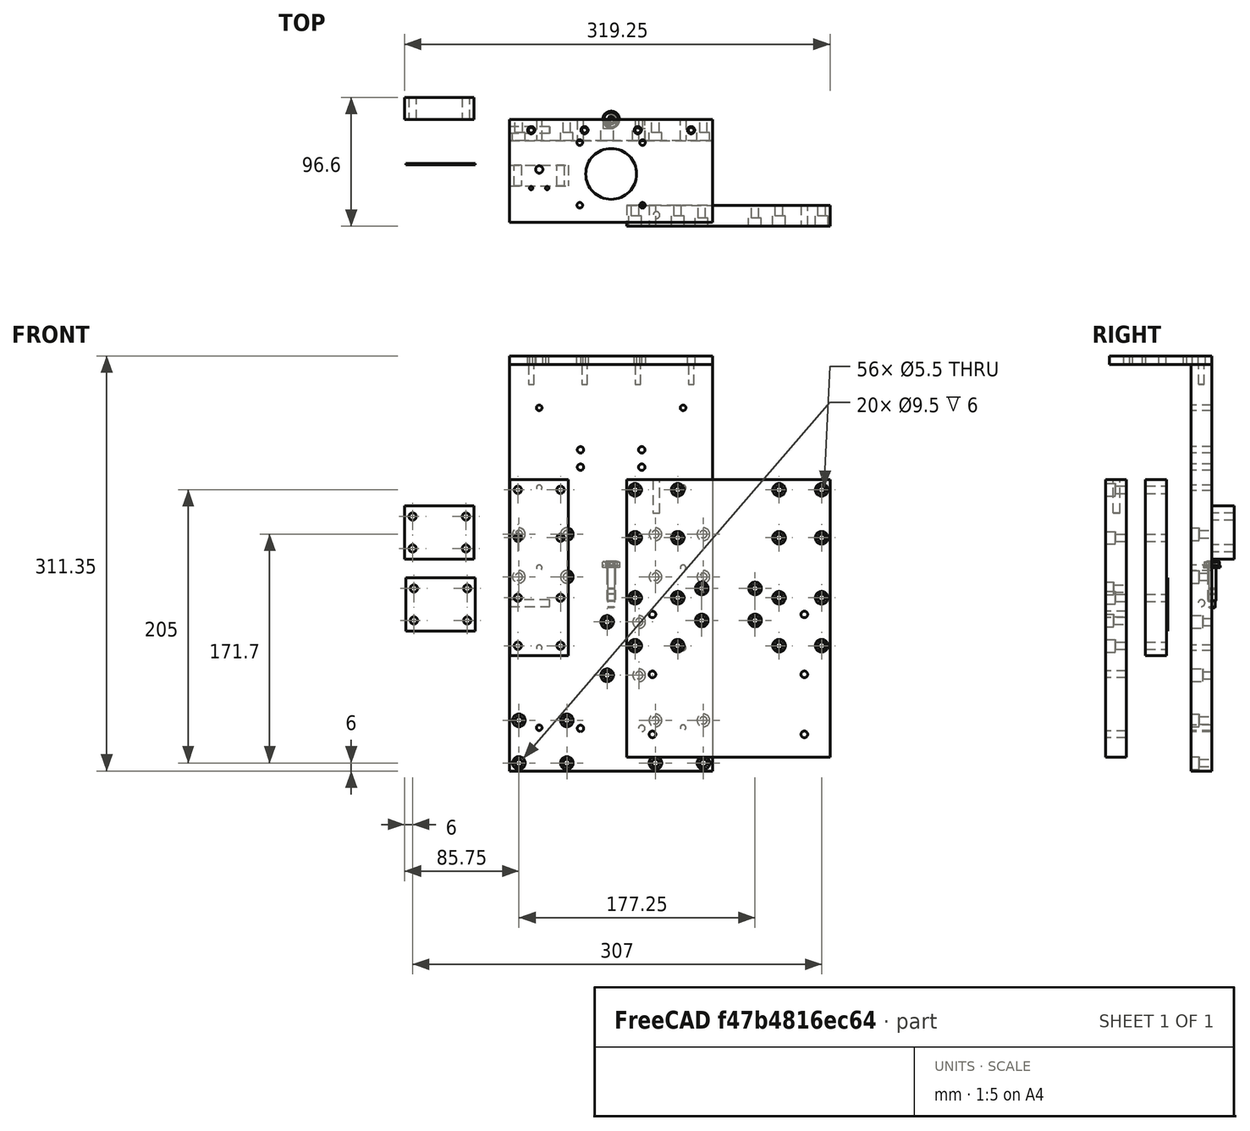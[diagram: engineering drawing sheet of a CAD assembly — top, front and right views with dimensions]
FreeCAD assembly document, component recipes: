
FREECAD ASSEMBLY — COMPONENT RECIPES ("Z axis plates")

This assembly document has 16 components, labeled P0..P15 below (a component is one placed body or linked part). 6 of them carry a construction recipe — the FreeCAD feature program that regenerates the part from scratch, quoted from this document or its linked companion documents; the rest are supplied as boundary geometry only. No exploded tour is included for this assembly.
COMPONENT P0 — recipe-attached ("Link(Backplate)", modeled in this document).
Construction recipe (the document's own serialized feature program — sketch geometry with constraints, then the solid features built on it; lengths are millimeters unless a unit is written):

FEATURE [Sketcher::SketchObject] Sketch
  FullyConstrained = true
  MapMode = 5
  Placement = pos=(0,0,0) rot=(1,0,0;1.5708rad)
  Support = -> [XZ_Plane]
  sketch-geometry (4):
    g0: LineSegment StartX=-76.25 StartY=152.5 StartZ=0 EndX=76.25 EndY=152.5 EndZ=0
    g1: LineSegment StartX=76.25 StartY=152.5 StartZ=0 EndX=76.25 EndY=-152.5 EndZ=0
    g2: LineSegment StartX=76.25 StartY=-152.5 StartZ=0 EndX=-76.25 EndY=-152.5 EndZ=0
    g3: LineSegment StartX=-76.25 StartY=-152.5 StartZ=0 EndX=-76.25 EndY=152.5 EndZ=0
  constraints (11):
    c: Coincident(g0,g1)
    c: Coincident(g1,g2)
    c: Coincident(g2,g3)
    c: Coincident(g3,g0)
    c: Horizontal(g0)
    c: Horizontal(g2)
    c: Vertical(g1)
    c: Vertical(g3)
    c: Symmetric(g1,g0,g-1)
    c: DistanceX(g0,g0) = 152.5
    c: DistanceY(g1,g1) = 305
FEATURE [PartDesign::Pad] Pad
  ClaimChildren = false
  Direction = (1,1,1)
  Fit = 0
  FitJoin = 0
  InnerFit = 0
  InnerFitJoin = 0
  InnerTaperAngle = 0
  InnerTaperAngleRev = 0
  Length = 15.7
  Length2 = 100
  Linearize = true
  NewSolid = false
  Placement = pos=(0,0,0) rot=(1,0,0;1.5708rad)
  Profile = -> Sketch
  Refine = true
  Suppress = false
  Type = 0
  _ProfileBasedVersion = 0
FEATURE [Sketcher::SketchObject] Sketch001
  FullyConstrained = true
  MapMode = 5
  Placement = pos=(0,0,0) rot=(1,0,0;1.5708rad)
  Support = -> [XZ_Plane]
  sketch-geometry (9):
    g0: Circle CenterX=-54 CenterY=0 CenterZ=0 NormalX=0 NormalY=0 NormalZ=1 AngleXU=0 Radius=2.1
    g1: Circle CenterX=-54 CenterY=60 CenterZ=0 NormalX=0 NormalY=0 NormalZ=1 AngleXU=0 Radius=2.1
    g2: Circle CenterX=-54 CenterY=120 CenterZ=0 NormalX=0 NormalY=0 NormalZ=1 AngleXU=0 Radius=2.1
    g3: Circle CenterX=-54 CenterY=-60 CenterZ=0 NormalX=0 NormalY=0 NormalZ=1 AngleXU=0 Radius=2.1
    g4: Circle CenterX=-54 CenterY=-120 CenterZ=0 NormalX=0 NormalY=0 NormalZ=1 AngleXU=0 Radius=2.1
    g5: LineSegment [constr] StartX=-54 StartY=120 StartZ=0 EndX=-54 EndY=60 EndZ=0
    g6: LineSegment [constr] StartX=-54 StartY=60 StartZ=0 EndX=-54 EndY=0 EndZ=0
    g7: LineSegment [constr] StartX=-54 StartY=0 StartZ=0 EndX=-54 EndY=-60 EndZ=0
    g8: LineSegment [constr] StartX=-54 StartY=-60 StartZ=0 EndX=-54 EndY=-120 EndZ=0
  constraints (23):
    c: Vertical(g4,g3)
    c: Vertical(g3,g0)
    c: Vertical(g0,g1)
    c: Vertical(g1,g2)
    c: Equal(g2,g1)
    c: Equal(g1,g0)
    c: Equal(g0,g3)
    c: Equal(g3,g4)
    c: Coincident(g5,g2)
    c: Coincident(g5,g1)
    c: Coincident(g6,g1)
    c: Coincident(g6,g0)
    c: Coincident(g7,g0)
    c: Coincident(g7,g3)
    c: Coincident(g8,g3)
    c: Coincident(g8,g4)
    c: Equal(g8,g7)
    c: Equal(g7,g6)
    c: Equal(g6,g5)
    c: DistanceY(g5,g5) = 60
    c: DistanceX(g0,g-1) = 54
    c: PointOnObject(g0,g-1)
    c: Radius(g2) = 2.1
FEATURE [PartDesign::Pocket] Pocket
  BaseFeature = -> Pad
  ClaimChildren = false
  Fit = 0
  FitJoin = 0
  InnerFit = 0
  InnerFitJoin = 0
  InnerTaperAngle = 0
  InnerTaperAngleRev = 0
  Length = 5
  Length2 = 100
  Linearize = true
  Midplane = true
  NewSolid = false
  Placement = pos=(0,0,0) rot=(1,0,0;1.5708rad)
  Profile = -> Sketch001
  Refine = true
  Suppress = false
  Type = 1
  _ProfileBasedVersion = 0
FEATURE [PartDesign::Mirrored] Mirrored
  BaseFeature = -> Pocket
  CopyShape = false
  MirrorPlane = -> Sketch001 [V_Axis]
  NewSolid = false
  OriginalSubs = -> [Pocket]
  Originals = -> [Pocket]
  ParallelTransform = true
  Placement = pos=(0,0,0) rot=(1,0,0;1.5708rad)
  Refine = true
  SubTransform = true
  Suppress = false
  _Version = 1
FEATURE [Sketcher::SketchObject] Sketch002
  FullyConstrained = true
  MapMode = 5
  Placement = pos=(0,0,0) rot=(1,0,0;1.5708rad)
  Support = -> [XZ_Plane]
  sketch-geometry (8):
    g0: Circle CenterX=-23 CenterY=-120.525 CenterZ=0 NormalX=0 NormalY=0 NormalZ=1 AngleXU=0 Radius=2.4
    g1: Circle CenterX=23 CenterY=-120.525 CenterZ=0 NormalX=0 NormalY=0 NormalZ=1 AngleXU=0 Radius=2.4
    g2: LineSegment [constr] StartX=-23 StartY=-120.525 StartZ=0 EndX=23 EndY=-120.525 EndZ=0
    g3: GeomPoint [constr] X=0 Y=-120.525 Z=0
    g4: Circle CenterX=-23 CenterY=88.475 CenterZ=0 NormalX=0 NormalY=0 NormalZ=1 AngleXU=0 Radius=2.4
    g5: Circle CenterX=-23 CenterY=75.475 CenterZ=0 NormalX=0 NormalY=0 NormalZ=1 AngleXU=0 Radius=2.4
    g6: Circle CenterX=23 CenterY=88.475 CenterZ=0 NormalX=0 NormalY=0 NormalZ=1 AngleXU=0 Radius=2.4
    g7: Circle CenterX=23 CenterY=75.475 CenterZ=0 NormalX=0 NormalY=0 NormalZ=1 AngleXU=0 Radius=2.4
  constraints (21):
    c: Equal(g1,g0)
    c: Coincident(g2,g0)
    c: Coincident(g2,g1)
    c: Horizontal(g2)
    c: PointOnObject(g3,g-2)
    c: Symmetric(g0,g1,g3)
    c: Radius(g1) = 2.4
    c: DistanceX(g2,g2) = 46
    c: DistanceY(g3,g-1) = 120.525
    c: Equal(g6,g7)
    c: Equal(g7,g5)
    c: Equal(g5,g4)
    c: Equal(g4,g1)
    c: Vertical(g7,g6)
    c: Vertical(g6,g1)
    c: Vertical(g4,g5)
    c: Vertical(g5,g0)
    c: Horizontal(g4,g6)
    c: Horizontal(g5,g7)
    c: DistanceY(g7,g6) = 13
    c: DistanceY(g1,g7) = 196
FEATURE [PartDesign::Pocket] Pocket001
  BaseFeature = -> Mirrored
  ClaimChildren = false
  Fit = 0
  FitJoin = 0
  InnerFit = 0
  InnerFitJoin = 0
  InnerTaperAngle = 0
  InnerTaperAngleRev = 0
  Length = 5
  Length2 = 100
  Linearize = true
  Midplane = true
  NewSolid = false
  Placement = pos=(0,0,0) rot=(1,0,0;1.5708rad)
  Profile = -> Sketch002
  Refine = true
  Suppress = false
  Type = 1
  _ProfileBasedVersion = 0
FEATURE [Sketcher::SketchObject] Sketch009
  ExternalGeometry = -> [Pocket001]
  FullyConstrained = true
  MapMode = 5
  Placement = pos=(0,-15.7,-3.5e-15) rot=(1,0,0;1.5708rad)
  Support = -> [Pocket001]
  sketch-geometry (22):
    g0: Circle CenterX=-69.25 CenterY=-146.5 CenterZ=0 NormalX=0 NormalY=0 NormalZ=1 AngleXU=0 Radius=2.75
    g1: Circle CenterX=-69.25 CenterY=-114.5 CenterZ=0 NormalX=0 NormalY=0 NormalZ=1 AngleXU=0 Radius=2.75
    g2: Circle CenterX=-33.25 CenterY=-114.5 CenterZ=0 NormalX=0 NormalY=0 NormalZ=1 AngleXU=0 Radius=2.75
    g3: Circle CenterX=-33.25 CenterY=-146.5 CenterZ=0 NormalX=0 NormalY=0 NormalZ=1 AngleXU=0 Radius=2.75
    g4: Circle CenterX=33.25 CenterY=-114.5 CenterZ=0 NormalX=0 NormalY=0 NormalZ=1 AngleXU=0 Radius=2.75
    g5: Circle CenterX=69.25 CenterY=-114.5 CenterZ=0 NormalX=0 NormalY=0 NormalZ=1 AngleXU=0 Radius=2.75
    g6: Circle CenterX=33.25 CenterY=-146.5 CenterZ=0 NormalX=0 NormalY=0 NormalZ=1 AngleXU=0 Radius=2.75
    g7: Circle CenterX=69.25 CenterY=-146.5 CenterZ=0 NormalX=0 NormalY=0 NormalZ=1 AngleXU=0 Radius=2.75
    g8: LineSegment [constr] StartX=-69.25 StartY=-146.5 StartZ=0 EndX=-33.25 EndY=-146.5 EndZ=0
    g9: LineSegment [constr] StartX=33.25 StartY=-146.5 StartZ=0 EndX=69.25 EndY=-146.5 EndZ=0
    g10: Circle CenterX=-69.25 CenterY=-6.8 CenterZ=0 NormalX=0 NormalY=0 NormalZ=1 AngleXU=0 Radius=2.75
    g11: Circle CenterX=-69.25 CenterY=25.2 CenterZ=0 NormalX=0 NormalY=0 NormalZ=1 AngleXU=0 Radius=2.75
    g12: Circle CenterX=-33.25 CenterY=-6.8 CenterZ=0 NormalX=0 NormalY=0 NormalZ=1 AngleXU=0 Radius=2.75
    g13: Circle CenterX=-33.25 CenterY=25.2 CenterZ=0 NormalX=0 NormalY=0 NormalZ=1 AngleXU=0 Radius=2.75
    g14: Circle CenterX=33.25 CenterY=-6.8 CenterZ=0 NormalX=0 NormalY=0 NormalZ=1 AngleXU=0 Radius=2.75
    g15: Circle CenterX=33.25 CenterY=25.2 CenterZ=0 NormalX=0 NormalY=0 NormalZ=1 AngleXU=0 Radius=2.75
    g16: Circle CenterX=69.25 CenterY=-6.8 CenterZ=0 NormalX=0 NormalY=0 NormalZ=1 AngleXU=0 Radius=2.75
    g17: Circle CenterX=69.25 CenterY=25.2 CenterZ=0 NormalX=0 NormalY=0 NormalZ=1 AngleXU=0 Radius=2.75
    g18: GeomPoint [constr] X=69.25 Y=9.2 Z=0
    g19: GeomPoint [constr] X=69.25 Y=-130.5 Z=0
    g20: LineSegment [constr] StartX=-69.25 StartY=-146.5 StartZ=0 EndX=-69.25 EndY=-114.5 EndZ=0
    g21: LineSegment [constr] StartX=-69.25 StartY=25.2 StartZ=0 EndX=-69.25 EndY=-6.8 EndZ=0
  constraints (57):
    c: Horizontal(g5,g4)
    c: Horizontal(g4,g2)
    c: Horizontal(g2,g1)
    c: Horizontal(g0,g3)
    c: Horizontal(g6,g7)
    c: Vertical(g5,g7)
    c: Vertical(g4,g6)
    c: Vertical(g2,g3)
    c: Vertical(g1,g0)
    c: Equal(g1,g2)
    c: Equal(g2,g4)
    c: Equal(g4,g5)
    c: Equal(g5,g6)
    c: Equal(g6,g7)
    c: Equal(g7,g3)
    c: Equal(g3,g0)
    c: Diameter(g1) = 5.5
    c: Coincident(g8,g0)
    c: Coincident(g8,g3)
    c: Coincident(g9,g6)
    c: Coincident(g9,g7)
    c: Equal(g9,g8)
    c: DistanceY(g0,g1) = 32
    c: DistanceX(g8,g8) = 36
    c: Symmetric(g6,g3,g-2)
    c: DistanceY(g-3,g0) = 6
    c: DistanceX(g-3,g0) = 7
    c: Equal(g10,g12)
    c: Equal(g12,g14)
    c: Equal(g14,g16)
    c: Equal(g16,g17)
    c: Equal(g17,g15)
    c: Equal(g15,g13)
    c: Equal(g13,g11)
    c: Equal(g11,g1)
    c: Horizontal(g10,g12)
    c: Horizontal(g12,g14)
    c: Horizontal(g14,g16)
    c: Horizontal(g11,g13)
    c: Horizontal(g13,g15)
    c: Horizontal(g15,g17)
    c: Vertical(g10,g11)
    c: Vertical(g11,g1)
    c: Vertical(g12,g13)
    c: Vertical(g13,g2)
    c: Vertical(g14,g15)
    c: Vertical(g15,g4)
    c: Vertical(g16,g17)
    c: Vertical(g17,g5)
    c: Symmetric(g16,g17,g18)
    c: Symmetric(g5,g7,g19)
    c: DistanceY(g19,g18) = 139.7
    c: Coincident(g20,g0)
    c: Coincident(g20,g1)
    c: Coincident(g21,g11)
    c: Coincident(g21,g10)
    c: Equal(g21,g20)
FEATURE [PartDesign::Hole] Hole003
  BaseFeature = -> Pocket001
  ClaimChildren = false
  CustomThreadClearance = 0
  Depth = 25
  DepthType = 1
  Diameter = 5.5
  DrillForDepth = false
  DrillPoint = 1
  DrillPointAngle = 118
  Fit = 0
  FitJoin = 0
  HoleCutCountersinkAngle = 90
  HoleCutCustomValues = false
  HoleCutDepth = 6
  HoleCutDiameter = 9.5
  HoleCutType = 1
  InnerFit = 0
  InnerFitJoin = 0
  ModelThread = false
  NewSolid = false
  Placement = pos=(0,0,0) rot=(1,0,0;1.5708rad)
  Profile = -> Sketch009
  Refine = true
  Suppress = false
  Tapered = false
  TaperedAngle = 90
  ThreadClass = 0
  ThreadDepth = 689.55
  ThreadDepthType = 0
  ThreadDirection = 0
  ThreadFit = 0
  ThreadSize = 0
  ThreadType = 0
  Threaded = false
  UseCustomThreadClearance = false
  _ProfileBasedVersion = 0
FEATURE [Sketcher::SketchObject] Sketch011
  ExternalGeometry = -> [Hole003]
  FullyConstrained = true
  MapMode = 5
  Placement = pos=(0,0,152.5) rot=(0,0,1;3.14159rad)
  Support = -> [Hole003]
  sketch-geometry (9):
    g0: LineSegment [constr] StartX=-60 StartY=15.7 StartZ=0 EndX=-60 EndY=7.85 EndZ=0
    g1: LineSegment [constr] StartX=-60 StartY=7.85 StartZ=0 EndX=-60 EndY=0 EndZ=0
    g2: LineSegment [constr] StartX=-60 StartY=7.85 StartZ=0 EndX=-20 EndY=7.85 EndZ=0
    g3: LineSegment [constr] StartX=-20 StartY=7.85 StartZ=0 EndX=20 EndY=7.85 EndZ=0
    g4: LineSegment [constr] StartX=20 StartY=7.85 StartZ=0 EndX=60 EndY=7.85 EndZ=0
    g5: Circle CenterX=-60 CenterY=7.85 CenterZ=0 NormalX=0 NormalY=0 NormalZ=1 AngleXU=0 Radius=2.1
    g6: Circle CenterX=-20 CenterY=7.85 CenterZ=0 NormalX=0 NormalY=0 NormalZ=1 AngleXU=0 Radius=2.1
    g7: Circle CenterX=20 CenterY=7.85 CenterZ=0 NormalX=0 NormalY=0 NormalZ=1 AngleXU=0 Radius=2.1
    g8: Circle CenterX=60 CenterY=7.85 CenterZ=0 NormalX=0 NormalY=0 NormalZ=1 AngleXU=0 Radius=2.1
  constraints (23):
    c: PointOnObject(g0,g-3)
    c: Vertical(g0)
    c: Coincident(g1,g0)
    c: PointOnObject(g1,g-1)
    c: Coincident(g2,g0)
    c: Horizontal(g2)
    c: Coincident(g3,g2)
    c: Coincident(g4,g3)
    c: Horizontal(g4)
    c: Vertical(g1)
    c: Equal(g1,g0)
    c: Equal(g2,g3)
    c: Equal(g3,g4)
    c: Symmetric(g2,g3,g-2)
    c: Coincident(g5,g0)
    c: Coincident(g6,g2)
    c: Coincident(g7,g3)
    c: Coincident(g8,g4)
    c: Equal(g8,g7)
    c: Equal(g7,g6)
    c: Equal(g6,g5)
    c: Diameter(g8) = 4.2
    c: DistanceX(g3,g3) = 40
FEATURE [PartDesign::Pocket] Pocket002
  BaseFeature = -> Hole003
  ClaimChildren = false
  Fit = 0
  FitJoin = 0
  InnerFit = 0
  InnerFitJoin = 0
  InnerTaperAngle = 0
  InnerTaperAngleRev = 0
  Length = 15
  Length2 = 100
  Linearize = true
  NewSolid = false
  Placement = pos=(0,0,0) rot=(1,0,0;1.5708rad)
  Profile = -> Sketch011
  Refine = true
  Suppress = false
  Type = 0
  _ProfileBasedVersion = 0
FEATURE [Sketcher::SketchObject] Sketch013
  ExternalGeometry = -> [Pocket002]
  FullyConstrained = true
  MapMode = 5
  Placement = pos=(0,-15.7,-3.5e-15) rot=(1,0,0;1.5708rad)
  Support = -> [Pocket002]
  sketch-geometry (6):
    g0: Circle CenterX=-3 CenterY=-40.65 CenterZ=0 NormalX=0 NormalY=0 NormalZ=1 AngleXU=0 Radius=2.75
    g1: Circle CenterX=21 CenterY=-40.65 CenterZ=0 NormalX=0 NormalY=0 NormalZ=1 AngleXU=0 Radius=2.75
    g2: Circle CenterX=-3 CenterY=-80.65 CenterZ=0 NormalX=0 NormalY=0 NormalZ=1 AngleXU=0 Radius=2.75
    g3: Circle CenterX=21 CenterY=-80.65 CenterZ=0 NormalX=0 NormalY=0 NormalZ=1 AngleXU=0 Radius=2.75
    g4: GeomPoint [constr] X=33.25 Y=-60.65 Z=0
    g5: GeomPoint [constr] X=21 Y=-60.65 Z=0
  constraints (14):
    c: Equal(g0,g1)
    c: Equal(g1,g3)
    c: Equal(g3,g2)
    c: Vertical(g1,g3)
    c: Vertical(g0,g2)
    c: Horizontal(g2,g3)
    c: DistanceX(g0,g1) = 24
    c: DistanceY(g3,g1) = 40
    c: Horizontal(g4,g5)
    c: Symmetric(g1,g3,g5)
    c: Symmetric(g-4,g-3,g4)
    c: Diameter(g0) = 5.5
    c: DistanceX(g-1,g1) = 21
    c: Horizontal(g0,g1)
FEATURE [PartDesign::Hole] Hole004
  BaseFeature = -> Pocket002
  ClaimChildren = false
  CustomThreadClearance = 0
  Depth = 25
  DepthType = 1
  Diameter = 5.5
  DrillForDepth = false
  DrillPoint = 1
  DrillPointAngle = 118
  Fit = 0
  FitJoin = 0
  HoleCutCountersinkAngle = 90
  HoleCutCustomValues = false
  HoleCutDepth = 9
  HoleCutDiameter = 9.5
  HoleCutType = 1
  InnerFit = 0
  InnerFitJoin = 0
  ModelThread = false
  NewSolid = false
  Placement = pos=(0,0,0) rot=(1,0,0;1.5708rad)
  Profile = -> Sketch013
  Refine = true
  Suppress = false
  Tapered = false
  TaperedAngle = 90
  ThreadClass = 0
  ThreadDepth = 689.55
  ThreadDepthType = 0
  ThreadDirection = 0
  ThreadFit = 0
  ThreadSize = 0
  ThreadType = 0
  Threaded = false
  UseCustomThreadClearance = false
  _ProfileBasedVersion = 0
FEATURE [Sketcher::SketchObject] Sketch014
  ExternalGeometry = -> [Hole004]
  FullyConstrained = true
  MapMode = 5
  Placement = pos=(-76.25,0,0) rot=(0.707107,0,-0.707107;3.14159rad)
  Support = -> [Hole004]
  sketch-geometry (3):
    g0: Circle CenterX=26.5 CenterY=7.85 CenterZ=0 NormalX=0 NormalY=0 NormalZ=1 AngleXU=0 Radius=2.5
    g1: GeomPoint [constr] X=26.5 Y=15.7 Z=0
    g2: GeomPoint [constr] X=26.5 Y=0 Z=0
  constraints (6):
    c: PointOnObject(g1,g-3)
    c: PointOnObject(g2,g-1)
    c: Vertical(g1,g0)
    c: DistanceX(g-3,g1) = 179
    c: Symmetric(g1,g2,g0)
    c: Diameter(g0) = 5
FEATURE [PartDesign::Pocket] Pocket004
  BaseFeature = -> Hole004
  ClaimChildren = false
  Fit = 0
  FitJoin = 0
  InnerFit = 0
  InnerFitJoin = 0
  InnerTaperAngle = 0
  InnerTaperAngleRev = 0
  Length = 30
  Length2 = 100
  Linearize = true
  NewSolid = false
  Placement = pos=(0,0,0) rot=(1,0,0;1.5708rad)
  Profile = -> Sketch014
  Refine = true
  Suppress = false
  Type = 0
  _ProfileBasedVersion = 1
FEATURE [PartDesign::Body] Body  label="Backplate"
  AutoGroupSolids = false
  ExportMode = 0
  Group = -> [Sketch,Pad,Sketch001,Pocket,Mirrored,Sketch002,Pocket001,Sketch009,Hole003,Sketch011,Pocket002,Sketch013,Hole004,Sketch014,Pocket004]
  Origin = -> Origin
  Tip = -> Pocket004
  _ExportChildren = -> [Pad,Pocket,Mirrored,Pocket001,Hole003,Pocket002,Hole004,Pocket004]
  _GroupVersion = 1
COMPONENT P1 — recipe-attached ("Link001(Shim)", modeled in this document).
Construction recipe (the document's own serialized feature program — sketch geometry with constraints, then the solid features built on it; lengths are millimeters unless a unit is written):

FEATURE [PartDesign::ShapeBinder] ShapeBinder001
  Placement = pos=(0,0,0) rot=(1,0,0;1.5708rad)
  Support = -> [Hole001]
  TraceSupport = false
FEATURE [Sketcher::SketchObject] Sketch006
  ExternalGeometry = -> [ShapeBinder001]
  FullyConstrained = true
  MapMode = 5
  Placement = pos=(0,0,0) rot=(1,0,0;1.5708rad)
  Support = -> [XZ_Plane002]
  sketch-geometry (16):
    g0: LineSegment StartX=-76 StartY=66 StartZ=0 EndX=-32 EndY=66 EndZ=0
    g1: LineSegment StartX=-32 StartY=66 StartZ=0 EndX=-32 EndY=-66 EndZ=0
    g2: LineSegment StartX=-32 StartY=-66 StartZ=0 EndX=-76 EndY=-66 EndZ=0
    g3: LineSegment StartX=-76 StartY=-66 StartZ=0 EndX=-76 EndY=66 EndZ=0
    g4: LineSegment [constr] StartX=-70 StartY=58.5 StartZ=0 EndX=-76 EndY=58.5 EndZ=0
    g5: LineSegment [constr] StartX=-38 StartY=58.5 StartZ=0 EndX=-32 EndY=58.5 EndZ=0
    g6: LineSegment [constr] StartX=-38 StartY=58.5 StartZ=0 EndX=-38 EndY=66 EndZ=0
    g7: LineSegment [constr] StartX=-38 StartY=-58.5 StartZ=0 EndX=-38 EndY=-66 EndZ=0
    g8: Circle CenterX=-70 CenterY=58.5 CenterZ=0 NormalX=0 NormalY=0 NormalZ=1 AngleXU=0 Radius=2.75
    g9: Circle CenterX=-38 CenterY=58.5 CenterZ=0 NormalX=0 NormalY=0 NormalZ=1 AngleXU=0 Radius=2.75
    g10: Circle CenterX=-70 CenterY=22.5 CenterZ=0 NormalX=0 NormalY=0 NormalZ=1 AngleXU=0 Radius=2.75
    g11: Circle CenterX=-38 CenterY=22.5 CenterZ=0 NormalX=0 NormalY=0 NormalZ=1 AngleXU=0 Radius=2.75
    g12: Circle CenterX=-70 CenterY=-22.5 CenterZ=0 NormalX=0 NormalY=0 NormalZ=1 AngleXU=0 Radius=2.75
    g13: Circle CenterX=-38 CenterY=-22.5 CenterZ=0 NormalX=0 NormalY=0 NormalZ=1 AngleXU=0 Radius=2.75
    g14: Circle CenterX=-70 CenterY=-58.5 CenterZ=0 NormalX=0 NormalY=0 NormalZ=1 AngleXU=0 Radius=2.75
    g15: Circle CenterX=-38 CenterY=-58.5 CenterZ=0 NormalX=0 NormalY=0 NormalZ=1 AngleXU=0 Radius=2.75
  constraints (40):
    c: Coincident(g0,g1)
    c: Coincident(g1,g2)
    c: Coincident(g2,g3)
    c: Coincident(g3,g0)
    c: Horizontal(g0)
    c: Horizontal(g2)
    c: Vertical(g1)
    c: Vertical(g3)
    c: DistanceX(g2,g2) = 44
    c: DistanceY(g1,g1) = 132
    c: Coincident(g4,g-3)
    c: PointOnObject(g4,g3)
    c: Horizontal(g4)
    c: Coincident(g5,g-4)
    c: PointOnObject(g5,g1)
    c: Horizontal(g5)
    c: Equal(g5,g4)
    c: Coincident(g6,g-4)
    c: PointOnObject(g6,g0)
    c: Coincident(g7,g-10)
    c: PointOnObject(g7,g2)
    c: Vertical(g7)
    c: Vertical(g6)
    c: Equal(g6,g7)
    c: Coincident(g8,g-3)
    c: Coincident(g9,g-4)
    c: Coincident(g10,g-5)
    c: Coincident(g11,g-6)
    c: Coincident(g12,g-7)
    c: Coincident(g13,g-8)
    c: Coincident(g14,g-9)
    c: Coincident(g15,g-10)
    c: Equal(g15,g14)
    c: Equal(g14,g12)
    c: Equal(g12,g13)
    c: Equal(g13,g10)
    c: Equal(g10,g11)
    c: Equal(g11,g8)
    c: Equal(g8,g9)
    c: Equal(g9,g-4)
FEATURE [PartDesign::Pad] Pad002
  ClaimChildren = false
  Direction = (1,1,1)
  Fit = 0
  FitJoin = 0
  InnerFit = 0
  InnerFitJoin = 0
  InnerTaperAngle = 0
  InnerTaperAngleRev = 0
  Length = 15.7
  Length2 = 100
  Linearize = true
  Midplane = true
  NewSolid = false
  Placement = pos=(0,0,0) rot=(1,0,0;1.5708rad)
  Profile = -> Sketch006
  Refine = true
  Suppress = false
  Type = 0
  _ProfileBasedVersion = 0
FEATURE [PartDesign::Body] Body002  label="Shim"
  AutoGroupSolids = false
  ExportMode = 0
  Group = -> [ShapeBinder001,Sketch006,Pad002]
  Origin = -> Origin002
  Placement = pos=(0,-42,0) rot=(0,0,1;0rad)
  Tip = -> Pad002
  _ExportChildren = -> [ShapeBinder001,Pad002]
  _GroupVersion = 1
COMPONENT P2 — recipe-attached ("Link002(Frontplate)", modeled in this document).
Construction recipe (the document's own serialized feature program — sketch geometry with constraints, then the solid features built on it; lengths are millimeters unless a unit is written):

FEATURE [PartDesign::ShapeBinder] ShapeBinder
  Placement = pos=(0,0,0) rot=(1,0,0;1.5708rad)
  Support = -> [Pocket001]
  TraceSupport = false
FEATURE [Sketcher::SketchObject] Sketch003
  FullyConstrained = true
  MapMode = 5
  Placement = pos=(0,0,0) rot=(1,0,0;1.5708rad)
  Support = -> [XZ_Plane001]
  sketch-geometry (4):
    g0: LineSegment StartX=-76.25 StartY=66 StartZ=0 EndX=76.25 EndY=66 EndZ=0
    g1: LineSegment StartX=76.25 StartY=66 StartZ=0 EndX=76.25 EndY=-142 EndZ=0
    g2: LineSegment StartX=76.25 StartY=-142 StartZ=0 EndX=-76.25 EndY=-142 EndZ=0
    g3: LineSegment StartX=-76.25 StartY=-142 StartZ=0 EndX=-76.25 EndY=66 EndZ=0
  constraints (11):
    c: Coincident(g0,g1)
    c: Coincident(g1,g2)
    c: Coincident(g2,g3)
    c: Coincident(g3,g0)
    c: Horizontal(g2)
    c: Vertical(g1)
    c: Vertical(g3)
    c: DistanceX(g0,g0) = 152.5
    c: DistanceY(g1,g1) = 208
    c: Symmetric(g0,g0,g-2)
    c: DistanceY(g-1,g0) = 66
FEATURE [PartDesign::Pad] Pad001
  ClaimChildren = false
  Direction = (1,1,1)
  Fit = 0
  FitJoin = 0
  InnerFit = 0
  InnerFitJoin = 0
  InnerTaperAngle = 0
  InnerTaperAngleRev = 0
  Length = 15.7
  Length2 = 100
  Linearize = true
  Midplane = true
  NewSolid = false
  Placement = pos=(0,0,0) rot=(1,0,0;1.5708rad)
  Profile = -> Sketch003
  Refine = true
  Suppress = false
  Type = 0
  _ProfileBasedVersion = 0
FEATURE [Sketcher::SketchObject] Sketch004
  ExternalGeometry = -> [ShapeBinder]
  FullyConstrained = true
  MapMode = 5
  Placement = pos=(0,-7.85,-1.7e-15) rot=(1,0,0;1.5708rad)
  Support = -> [Pad001]
  sketch-geometry (21):
    g0: Circle CenterX=-70 CenterY=58.5 CenterZ=0 NormalX=0 NormalY=0 NormalZ=1 AngleXU=0 Radius=2.75
    g1: Circle CenterX=-38 CenterY=58.5 CenterZ=0 NormalX=0 NormalY=0 NormalZ=1 AngleXU=0 Radius=2.75
    g2: Circle CenterX=-70 CenterY=22.5 CenterZ=0 NormalX=0 NormalY=0 NormalZ=1 AngleXU=0 Radius=2.75
    g3: Circle CenterX=-38 CenterY=22.5 CenterZ=0 NormalX=0 NormalY=0 NormalZ=1 AngleXU=0 Radius=2.75
    g4: Circle CenterX=-70 CenterY=-22.5 CenterZ=0 NormalX=0 NormalY=0 NormalZ=1 AngleXU=0 Radius=2.75
    g5: Circle CenterX=-38 CenterY=-22.5 CenterZ=0 NormalX=0 NormalY=0 NormalZ=1 AngleXU=0 Radius=2.75
    g6: Circle CenterX=-70 CenterY=-58.5 CenterZ=0 NormalX=0 NormalY=0 NormalZ=1 AngleXU=0 Radius=2.75
    g7: Circle CenterX=-38 CenterY=-58.5 CenterZ=0 NormalX=0 NormalY=0 NormalZ=1 AngleXU=0 Radius=2.75
    g8: Circle CenterX=38 CenterY=-22.5 CenterZ=0 NormalX=0 NormalY=0 NormalZ=1 AngleXU=0 Radius=2.75
    g9: Circle CenterX=70 CenterY=-22.5 CenterZ=0 NormalX=0 NormalY=0 NormalZ=1 AngleXU=0 Radius=2.75
    g10: Circle CenterX=38 CenterY=-58.5 CenterZ=0 NormalX=0 NormalY=0 NormalZ=1 AngleXU=0 Radius=2.75
    g11: Circle CenterX=70 CenterY=-58.5 CenterZ=0 NormalX=0 NormalY=0 NormalZ=1 AngleXU=0 Radius=2.75
    g12: Circle CenterX=38 CenterY=22.5 CenterZ=0 NormalX=0 NormalY=0 NormalZ=1 AngleXU=0 Radius=2.75
    g13: Circle CenterX=70 CenterY=22.5 CenterZ=0 NormalX=0 NormalY=0 NormalZ=1 AngleXU=0 Radius=2.75
    g14: Circle CenterX=38 CenterY=58.5 CenterZ=0 NormalX=0 NormalY=0 NormalZ=1 AngleXU=0 Radius=2.75
    g15: Circle CenterX=70 CenterY=58.5 CenterZ=0 NormalX=0 NormalY=0 NormalZ=1 AngleXU=0 Radius=2.75
    g16: LineSegment [constr] StartX=-70 StartY=58.5 StartZ=0 EndX=-70 EndY=22.5 EndZ=0
    g17: LineSegment [constr] StartX=-70 StartY=-22.5 StartZ=0 EndX=-70 EndY=-58.5 EndZ=0
    g18: LineSegment [constr] StartX=-70 StartY=58.5 StartZ=0 EndX=-38 EndY=58.5 EndZ=0
    g19: LineSegment [constr] StartX=38 StartY=58.5 StartZ=0 EndX=70 EndY=58.5 EndZ=0
    g20: GeomPoint [constr] X=-54 Y=58.5 Z=0
  constraints (56):
    c: Horizontal(g0,g1)
    c: Horizontal(g1,g14)
    c: Horizontal(g14,g15)
    c: Horizontal(g2,g3)
    c: Horizontal(g3,g12)
    c: Horizontal(g12,g13)
    c: Horizontal(g4,g5)
    c: Horizontal(g5,g8)
    c: Horizontal(g8,g9)
    c: Horizontal(g6,g7)
    c: Horizontal(g7,g10)
    c: Horizontal(g10,g11)
    c: Equal(g0,g1)
    c: Equal(g1,g14)
    c: Equal(g14,g15)
    c: Equal(g15,g12)
    c: Equal(g12,g13)
    c: Equal(g13,g3)
    c: Equal(g3,g2)
    c: Equal(g2,g4)
    c: Equal(g4,g5)
    c: Equal(g5,g8)
    c: Equal(g8,g9)
    c: Equal(g9,g10)
    c: Equal(g10,g11)
    c: Equal(g11,g7)
    c: Equal(g7,g6)
    c: Vertical(g0,g2)
    c: Vertical(g2,g4)
    c: Vertical(g4,g6)
    c: Vertical(g7,g5)
    c: Vertical(g5,g3)
    c: Vertical(g3,g1)
    c: Vertical(g14,g12)
    c: Vertical(g12,g8)
    c: Vertical(g8,g10)
    c: Vertical(g15,g13)
    c: Vertical(g13,g9)
    c: Vertical(g9,g11)
    c: Coincident(g16,g0)
    c: Coincident(g16,g2)
    c: Coincident(g17,g4)
    c: Coincident(g17,g6)
    c: Coincident(g18,g0)
    c: Coincident(g18,g1)
    c: Coincident(g19,g14)
    c: Coincident(g19,g15)
    c: Equal(g18,g19)
    c: Equal(g16,g17)
    c: Symmetric(g2,g9,g-1)
    c: DistanceX(g18,g18) = 32
    c: DistanceY(g16,g16) = 36
    c: Diameter(g15) = 5.5
    c: DistanceY(g4,g2) = 45
    c: Vertical(g20,g-3)
    c: Symmetric(g0,g1,g20)
FEATURE [PartDesign::Hole] Hole  label="Carriages mounts"
  BaseFeature = -> Pad001
  ClaimChildren = false
  CustomThreadClearance = 0
  Depth = 25
  DepthType = 1
  Diameter = 5.5
  DrillForDepth = false
  DrillPoint = 1
  DrillPointAngle = 118
  Fit = 0
  FitJoin = 0
  HoleCutCountersinkAngle = 90
  HoleCutCustomValues = false
  HoleCutDepth = 7.5
  HoleCutDiameter = 9.5
  HoleCutType = 1
  InnerFit = 0
  InnerFitJoin = 0
  ModelThread = false
  NewSolid = false
  Placement = pos=(0,0,0) rot=(1,0,0;1.5708rad)
  Profile = -> Sketch004
  Refine = true
  Suppress = false
  Tapered = false
  TaperedAngle = 90
  ThreadClass = 0
  ThreadDepth = 444.18
  ThreadDepthType = 0
  ThreadDirection = 0
  ThreadFit = 0
  ThreadSize = 0
  ThreadType = 0
  Threaded = false
  UseCustomThreadClearance = false
  _ProfileBasedVersion = 0
FEATURE [Sketcher::SketchObject] Sketch005
  FullyConstrained = true
  MapMode = 5
  Placement = pos=(0,-7.85,-1.7e-15) rot=(1,0,0;1.5708rad)
  Support = -> [Hole]
  sketch-geometry (4):
    g0: Circle CenterX=-20 CenterY=-15.525 CenterZ=0 NormalX=0 NormalY=0 NormalZ=1 AngleXU=0 Radius=2.75
    g1: Circle CenterX=20 CenterY=-15.525 CenterZ=0 NormalX=0 NormalY=0 NormalZ=1 AngleXU=0 Radius=2.75
    g2: Circle CenterX=-20 CenterY=-39.525 CenterZ=0 NormalX=0 NormalY=0 NormalZ=1 AngleXU=0 Radius=2.75
    g3: Circle CenterX=20 CenterY=-39.525 CenterZ=0 NormalX=0 NormalY=0 NormalZ=1 AngleXU=0 Radius=2.75
  constraints (11):
    c: Horizontal(g2,g3)
    c: Vertical(g0,g2)
    c: Vertical(g1,g3)
    c: DistanceX(g0,g1) = 40
    c: DistanceY(g3,g1) = 24
    c: Diameter(g0) = 5.5
    c: Equal(g0,g1)
    c: Equal(g1,g3)
    c: Equal(g3,g2)
    c: DistanceY(g1,g-1) = 15.525
    c: Symmetric(g1,g0,g-2)
FEATURE [PartDesign::Hole] Hole001  label="Screw mount"
  BaseFeature = -> Hole
  ClaimChildren = false
  CustomThreadClearance = 0
  Depth = 25
  DepthType = 1
  Diameter = 5.5
  DrillForDepth = false
  DrillPoint = 1
  DrillPointAngle = 118
  Fit = 0
  FitJoin = 0
  HoleCutCountersinkAngle = 90
  HoleCutCustomValues = false
  HoleCutDepth = 6
  HoleCutDiameter = 9.5
  HoleCutType = 1
  InnerFit = 0
  InnerFitJoin = 0
  ModelThread = false
  NewSolid = false
  Placement = pos=(0,0,0) rot=(1,0,0;1.5708rad)
  Profile = -> Sketch005
  Refine = true
  Suppress = false
  Tapered = false
  TaperedAngle = 90
  ThreadClass = 0
  ThreadDepth = 444.18
  ThreadDepthType = 0
  ThreadDirection = 0
  ThreadFit = 0
  ThreadSize = 0
  ThreadType = 0
  Threaded = false
  UseCustomThreadClearance = false
  _ProfileBasedVersion = 0
FEATURE [Sketcher::SketchObject] Sketch012
  ExternalGeometry = -> [Pad001]
  FullyConstrained = true
  MapMode = 5
  Placement = pos=(0,-7.85,-1.7e-15) rot=(1,0,0;1.5708rad)
  sketch-geometry (6):
    g0: Circle CenterX=-57 CenterY=-80 CenterZ=0 NormalX=0 NormalY=0 NormalZ=1 AngleXU=0 Radius=2.5
    g1: Circle CenterX=-57 CenterY=-125 CenterZ=0 NormalX=0 NormalY=0 NormalZ=1 AngleXU=0 Radius=2.5
    g2: Circle CenterX=57 CenterY=-80 CenterZ=0 NormalX=0 NormalY=0 NormalZ=1 AngleXU=0 Radius=2.5
    g3: Circle CenterX=57 CenterY=-125 CenterZ=0 NormalX=0 NormalY=0 NormalZ=1 AngleXU=0 Radius=2.5
    g4: Circle CenterX=-57 CenterY=-35 CenterZ=0 NormalX=0 NormalY=0 NormalZ=1 AngleXU=0 Radius=2.5
    g5: Circle CenterX=57 CenterY=-35 CenterZ=0 NormalX=0 NormalY=0 NormalZ=1 AngleXU=0 Radius=2.5
  constraints (17):
    c: Vertical(g0,g1)
    c: Horizontal(g1,g3)
    c: Equal(g1,g0)
    c: Equal(g0,g2)
    c: Equal(g2,g3)
    c: Diameter(g2) = 5
    c: Symmetric(g2,g0,g-2)
    c: DistanceX(g0,g2) = 114
    c: DistanceY(g1,g0) = 45
    c: Vertical(g3,g2)
    c: DistanceY(g-3,g3) = 17
    c: Vertical(g5,g2)
    c: Vertical(g4,g0)
    c: Horizontal(g4,g5)
    c: Equal(g4,g5)
    c: Equal(g5,g2)
    c: DistanceY(g0,g4) = 45
FEATURE [PartDesign::Pocket] Pocket003
  BaseFeature = -> Hole001
  ClaimChildren = false
  Fit = 0
  FitJoin = 0
  InnerFit = 0
  InnerFitJoin = 0
  InnerTaperAngle = 0
  InnerTaperAngleRev = 0
  Length = 5
  Length2 = 100
  Linearize = true
  NewSolid = false
  Placement = pos=(0,0,0) rot=(1,0,0;1.5708rad)
  Profile = -> Sketch012
  Refine = true
  Suppress = false
  Type = 1
  _ProfileBasedVersion = 0
FEATURE [Sketcher::SketchObject] Sketch016
  FullyConstrained = true
  MapMode = 5
  Placement = pos=(0,0,66) rot=(0,0,1;3.14159rad)
  Support = -> [Pocket003]
  sketch-geometry (1):
    g0: Circle CenterX=54 CenterY=-0.4 CenterZ=0 NormalX=0 NormalY=0 NormalZ=1 AngleXU=0 Radius=2.5
  constraints (3):
    c: Diameter(g0) = 5
    c: DistanceX(g-1,g0) = 54
    c: DistanceY(g0,g-1) = 0.4
FEATURE [PartDesign::Pocket] Pocket006
  BaseFeature = -> Pocket003
  ClaimChildren = false
  Fit = 0
  FitJoin = 0
  InnerFit = 0
  InnerFitJoin = 0
  InnerTaperAngle = 0
  InnerTaperAngleRev = 0
  Length = 25
  Length2 = 100
  Linearize = true
  NewSolid = false
  Placement = pos=(0,0,0) rot=(1,0,0;1.5708rad)
  Profile = -> Sketch016
  Refine = true
  Suppress = false
  Type = 0
  _ProfileBasedVersion = 1
FEATURE [PartDesign::Body] Body001  label="Frontplate"
  AutoGroupSolids = false
  ExportMode = 0
  Group = -> [ShapeBinder,Sketch003,Pad001,Sketch004,Hole,Sketch005,Hole001,Sketch012,Pocket003,Sketch016,Pocket006]
  Origin = -> Origin001
  Placement = pos=(88,-72,0) rot=(0,0,1;0rad)
  Tip = -> Pocket006
  _ExportChildren = -> [ShapeBinder,Pad001,Hole,Hole001,Pocket003,Pocket006]
  _GroupVersion = 1
COMPONENT P3 — recipe-attached ("Link003(Nut-shim)", modeled in this document).
Construction recipe (the document's own serialized feature program — sketch geometry with constraints, then the solid features built on it; lengths are millimeters unless a unit is written):

FEATURE [PartDesign::ShapeBinder] ShapeBinder002
  Placement = pos=(0,0,0) rot=(1,0,0;1.5708rad)
  TraceSupport = false
FEATURE [Sketcher::SketchObject] Sketch008
  ExternalGeometry = -> [ShapeBinder002]
  FullyConstrained = true
  MapMode = 5
  Placement = pos=(0,0,0) rot=(1,0,0;1.5708rad)
  Support = -> [XZ_Plane003]
  sketch-geometry (10):
    g0: LineSegment StartX=-26 StartY=-7.525 StartZ=0 EndX=26 EndY=-7.525 EndZ=0
    g1: LineSegment StartX=26 StartY=-7.525 StartZ=0 EndX=26 EndY=-47.525 EndZ=0
    g2: LineSegment StartX=26 StartY=-47.525 StartZ=0 EndX=-26 EndY=-47.525 EndZ=0
    g3: LineSegment StartX=-26 StartY=-47.525 StartZ=0 EndX=-26 EndY=-7.525 EndZ=0
    g4: Circle CenterX=20 CenterY=-39.525 CenterZ=0 NormalX=0 NormalY=0 NormalZ=1 AngleXU=0 Radius=2.75
    g5: Circle CenterX=-20 CenterY=-15.525 CenterZ=0 NormalX=0 NormalY=0 NormalZ=1 AngleXU=0 Radius=2.75
    g6: Circle CenterX=-20 CenterY=-39.525 CenterZ=0 NormalX=0 NormalY=0 NormalZ=1 AngleXU=0 Radius=2.75
    g7: Circle CenterX=20 CenterY=-15.525 CenterZ=0 NormalX=0 NormalY=0 NormalZ=1 AngleXU=0 Radius=2.75
    g8: LineSegment [constr] StartX=20 StartY=-15.525 StartZ=0 EndX=20 EndY=-7.525 EndZ=0
    g9: LineSegment [constr] StartX=20 StartY=-39.525 StartZ=0 EndX=20 EndY=-47.525 EndZ=0
  constraints (25):
    c: Coincident(g0,g1)
    c: Coincident(g1,g2)
    c: Coincident(g2,g3)
    c: Coincident(g3,g0)
    c: Horizontal(g2)
    c: Vertical(g1)
    c: Vertical(g3)
    c: DistanceX(g0,g0) = 52
    c: DistanceY(g1,g1) = 40
    c: Equal(g7,g6)
    c: Equal(g6,g4)
    c: Equal(g4,g5)
    c: Symmetric(g0,g0,g-2)
    c: Coincident(g5,g-3)
    c: Coincident(g7,g-4)
    c: Equal(g-4,g7)
    c: Coincident(g-5,g6)
    c: Coincident(g4,g-6)
    c: Coincident(g8,g7)
    c: PointOnObject(g8,g0)
    c: Vertical(g8)
    c: Coincident(g9,g4)
    c: PointOnObject(g9,g2)
    c: Vertical(g9)
    c: Equal(g9,g8)
FEATURE [PartDesign::Pad] Pad003
  ClaimChildren = false
  Direction = (1,1,1)
  Fit = 0
  FitJoin = 0
  InnerFit = 0
  InnerFitJoin = 0
  InnerTaperAngle = 0
  InnerTaperAngleRev = 0
  Length = 0.7
  Length2 = 100
  Linearize = true
  NewSolid = false
  Placement = pos=(0,0,0) rot=(1,0,0;1.5708rad)
  Profile = -> Sketch008
  Refine = true
  Suppress = false
  Type = 0
  _ProfileBasedVersion = 0
FEATURE [PartDesign::Body] Body003  label="Nut-shim"
  AutoGroupSolids = false
  ExportMode = 0
  Group = -> [ShapeBinder002,Sketch008,Pad003]
  Origin = -> Origin003
  Placement = pos=(-128,-33,0) rot=(0,0,1;0rad)
  Tip = -> Pad003
  _ExportChildren = -> [ShapeBinder002,Pad003]
  _GroupVersion = 1
COMPONENT P4 — recipe-attached ("Link004(Motor-bracket)", modeled in this document).
Construction recipe (the document's own serialized feature program — sketch geometry with constraints, then the solid features built on it; lengths are millimeters unless a unit is written):

FEATURE [PartDesign::ShapeBinder] ShapeBinder003
  Placement = pos=(0,0,0) rot=(1,0,0;1.5708rad)
  Support = -> [Pocket002]
  TraceSupport = false
FEATURE [Sketcher::SketchObject] Sketch010
  ExternalGeometry = -> [ShapeBinder003]
  FullyConstrained = true
  MapMode = 5
  Placement = pos=(0,-3.39e-14,152.5) rot=(0,0,1;3.14159rad)
  Support = -> [ShapeBinder003]
  sketch-geometry (19):
    g0: LineSegment StartX=-76.25 StartY=77.1 StartZ=0 EndX=76.25 EndY=77.1 EndZ=0
    g1: LineSegment StartX=76.25 StartY=77.1 StartZ=0 EndX=76.25 EndY=0 EndZ=0
    g2: LineSegment StartX=-76.25 StartY=0 StartZ=0 EndX=-76.25 EndY=77.1 EndZ=0
    g3: Circle CenterX=0 CenterY=40.7 CenterZ=0 NormalX=0 NormalY=0 NormalZ=1 AngleXU=0 Radius=19.05
    g4: Circle CenterX=-23.55 CenterY=64.25 CenterZ=0 NormalX=0 NormalY=0 NormalZ=1 AngleXU=0 Radius=2.1
    g5: Circle CenterX=23.55 CenterY=64.25 CenterZ=0 NormalX=0 NormalY=0 NormalZ=1 AngleXU=0 Radius=2.1
    g6: Circle CenterX=-23.55 CenterY=17.15 CenterZ=0 NormalX=0 NormalY=0 NormalZ=1 AngleXU=0 Radius=2.1
    g7: Circle CenterX=23.55 CenterY=17.15 CenterZ=0 NormalX=0 NormalY=0 NormalZ=1 AngleXU=0 Radius=2.1
    g8: LineSegment [constr] StartX=-23.55 StartY=64.25 StartZ=0 EndX=23.55 EndY=64.25 EndZ=0
    g9: LineSegment [constr] StartX=23.55 StartY=64.25 StartZ=0 EndX=23.55 EndY=17.15 EndZ=0
    g10: LineSegment [constr] StartX=-28.2 StartY=68.9 StartZ=0 EndX=28.2 EndY=68.9 EndZ=0
    g11: LineSegment [constr] StartX=28.2 StartY=68.9 StartZ=0 EndX=28.2 EndY=12.5 EndZ=0
    g12: LineSegment [constr] StartX=28.2 StartY=12.5 StartZ=0 EndX=-28.2 EndY=12.5 EndZ=0
    g13: LineSegment [constr] StartX=-28.2 StartY=12.5 StartZ=0 EndX=-28.2 EndY=68.9 EndZ=0
    g14: Circle CenterX=-60 CenterY=7.85 CenterZ=0 NormalX=0 NormalY=0 NormalZ=1 AngleXU=0 Radius=2.75
    g15: Circle CenterX=-20 CenterY=7.85 CenterZ=0 NormalX=0 NormalY=0 NormalZ=1 AngleXU=0 Radius=2.75
    g16: Circle CenterX=20 CenterY=7.85 CenterZ=0 NormalX=0 NormalY=0 NormalZ=1 AngleXU=0 Radius=2.75
    g17: Circle CenterX=60 CenterY=7.85 CenterZ=0 NormalX=0 NormalY=0 NormalZ=1 AngleXU=0 Radius=2.75
    g18: LineSegment StartX=-76.25 StartY=0 StartZ=0 EndX=76.25 EndY=0 EndZ=0
  constraints (48):
    c: Coincident(g0,g1)
    c: Coincident(g2,g0)
    c: Horizontal(g0)
    c: Vertical(g1)
    c: Vertical(g2)
    c: Symmetric(g2,g1,g-1)
    c: PointOnObject(g3,g-2)
    c: Diameter(g3) = 38.1
    c: Vertical(g7,g5)
    c: Vertical(g4,g6)
    c: Horizontal(g4,g5)
    c: Horizontal(g6,g7)
    c: Symmetric(g7,g4,g3)
    c: DistanceX(g4,g5) = 47.1
    c: Equal(g5,g4)
    c: Equal(g4,g6)
    c: Equal(g6,g7)
    c: Diameter(g5) = 4.2
    c: Coincident(g8,g4)
    c: Coincident(g8,g5)
    c: Coincident(g9,g5)
    c: Coincident(g9,g7)
    c: Equal(g9,g8)
    c: Coincident(g10,g11)
    c: Coincident(g11,g12)
    c: Coincident(g12,g13)
    c: Coincident(g13,g10)
    c: Horizontal(g10)
    c: Horizontal(g12)
    c: Vertical(g11)
    c: Vertical(g13)
    c: Symmetric(g10,g11,g3)
    c: Equal(g11,g10)
    c: DistanceY(g13,g13) = 56.4
    c: DistanceX(g0,g0) = 152.5
    c: DistanceY(g-4,g3) = 25
    c: Coincident(g14,g-5)
    c: Coincident(g15,g-6)
    c: Coincident(g16,g-7)
    c: Coincident(g17,g-8)
    c: Equal(g17,g16)
    c: Equal(g16,g15)
    c: Equal(g15,g14)
    c: Diameter(g14) = 5.5
    c: Coincident(g18,g2)
    c: Coincident(g18,g1)
    c: Horizontal(g18)
    c: DistanceY(g2,g2) = 77.1
FEATURE [PartDesign::Pad] Pad004
  ClaimChildren = false
  Direction = (1,1,1)
  Fit = 0
  FitJoin = 0
  InnerFit = 0
  InnerFitJoin = 0
  InnerTaperAngle = 0
  InnerTaperAngleRev = 0
  Length = 6.35
  Length2 = 100
  Linearize = true
  NewSolid = false
  Placement = pos=(0,0,0) rot=(1,0,0;1.5708rad)
  Profile = -> Sketch010
  Refine = true
  Suppress = false
  Type = 0
  _ProfileBasedVersion = 0
FEATURE [Sketcher::SketchObject] Sketch015
  FullyConstrained = true
  MapMode = 5
  Placement = pos=(0,-5.49e-14,152.5) rot=(1,0,0;3.14159rad)
  Support = -> [Pad004]
  sketch-geometry (5):
    g0: LineSegment [constr] StartX=-60 StartY=51.35 StartZ=0 EndX=-54 EndY=37.35 EndZ=0
    g1: LineSegment [constr] StartX=-54 StartY=37.35 StartZ=0 EndX=-48 EndY=51.35 EndZ=0
    g2: Circle CenterX=-48 CenterY=51.35 CenterZ=0 NormalX=0 NormalY=0 NormalZ=1 AngleXU=0 Radius=1.25
    g3: Circle CenterX=-60 CenterY=51.35 CenterZ=0 NormalX=0 NormalY=0 NormalZ=1 AngleXU=0 Radius=1.25
    g4: Circle CenterX=-54 CenterY=37.35 CenterZ=0 NormalX=0 NormalY=0 NormalZ=1 AngleXU=0 Radius=2.75
  constraints (13):
    c: Coincident(g1,g0)
    c: Equal(g1,g0)
    c: Coincident(g2,g1)
    c: Coincident(g3,g0)
    c: Coincident(g4,g0)
    c: Equal(g3,g2)
    c: Horizontal(g3,g2)
    c: Diameter(g3) = 2.5
    c: Diameter(g4) = 5.5
    c: DistanceX(g3,g2) = 12
    c: DistanceY(g4,g2) = 14
    c: DistanceX(g4,g-1) = 54
    c: DistanceY(g-1,g2) = 51.35
FEATURE [PartDesign::Pocket] Pocket005
  BaseFeature = -> Pad004
  ClaimChildren = false
  Fit = 0
  FitJoin = 0
  InnerFit = 0
  InnerFitJoin = 0
  InnerTaperAngle = 0
  InnerTaperAngleRev = 0
  Length = 5
  Length2 = 100
  Linearize = true
  NewSolid = false
  Placement = pos=(0,0,0) rot=(1,0,0;1.5708rad)
  Profile = -> Sketch015
  Refine = true
  Suppress = false
  Type = 1
  _ProfileBasedVersion = 1
FEATURE [PartDesign::Body] Body004  label="Motor-bracket"
  AutoGroupSolids = false
  ExportMode = 0
  Group = -> [Sketch010,Pad004,ShapeBinder003,Sketch015,Pocket005]
  Origin = -> Origin004
  Tip = -> Pocket005
  _ExportChildren = -> [Pad004,ShapeBinder003,Pocket005]
  _GroupVersion = 1
COMPONENT P5 — recipe-attached ("Link005(Nut-shim-X)", modeled in this document).
Construction recipe (the document's own serialized feature program — sketch geometry with constraints, then the solid features built on it; lengths are millimeters unless a unit is written):

FEATURE [PartDesign::ShapeBinder] ShapeBinder004
  Support = -> [Pad003]
  TraceSupport = false
FEATURE [PartDesign::Pad] Pad005
  ClaimChildren = false
  Direction = (1,1,1)
  Fit = 0
  FitJoin = 0
  InnerFit = 0
  InnerFitJoin = 0
  InnerTaperAngle = 0
  InnerTaperAngleRev = 0
  Length = 16.75
  Length2 = 100
  Linearize = true
  NewSolid = false
  Profile = -> ShapeBinder004
  Refine = true
  Suppress = false
  Type = 0
  _ProfileBasedVersion = 0
FEATURE [PartDesign::Body] Body005  label="Nut-shim-X"
  AutoGroupSolids = false
  ExportMode = 0
  Group = -> [ShapeBinder004,Pad005]
  Origin = -> Origin005
  Placement = pos=(-129,0,54) rot=(0,0,1;0rad)
  Tip = -> Pad005
  _ExportChildren = -> [Pad005]
  _GroupVersion = 1
COMPONENT P6 — geometry summary ("M5x16-Screw 16ct"; no construction recipe available for this part):
  bounding box: 180.2 x 147.0 x 21.0 mm
  tessellated surface: 90,784 triangles
  volume: 8792 mm^3 (2% of its bounding box)
  symmetry: 2-fold rotationally symmetric about the y axis; mirror-symmetric across its x mid-plane, z mid-plane
COMPONENT P7 — geometry summary ("M5x30-Screw 4ct"; no construction recipe available for this part):
  bounding box: 48.5 x 35.0 x 32.5 mm
  tessellated surface: 23,520 triangles
  volume: 3297 mm^3 (6% of its bounding box)
  symmetry: 2-fold rotationally symmetric about the y axis; mirror-symmetric across its x mid-plane, z mid-plane
COMPONENT P8 — geometry summary ("M5x20-Screw 4ct"; no construction recipe available for this part):
  bounding box: 128.5 x 25.0 x 8.5 mm
  tessellated surface: 22,696 triangles
  volume: 2512 mm^3 (9% of its bounding box)
  symmetry: 2-fold rotationally symmetric about the z axis; mirror-symmetric across its x mid-plane, y mid-plane
COMPONENT P9 — geometry summary ("M5x30-Screw 16ct"; no construction recipe available for this part):
  bounding box: 148.5 x 125.5 x 35.0 mm
  tessellated surface: 94,080 triangles
  volume: 13190 mm^3 (2% of its bounding box)
  symmetry: 2-fold rotationally symmetric about the y axis; mirror-symmetric across its x mid-plane, z mid-plane
COMPONENT P10 — geometry summary ("M5x16-Screw 4ct "; no construction recipe available for this part):
  bounding box: 48.5 x 32.5 x 21.0 mm
  tessellated surface: 22,696 triangles
  volume: 2198 mm^3 (7% of its bounding box)
  symmetry: 2-fold rotationally symmetric about the y axis; mirror-symmetric across its x mid-plane
COMPONENT P11 — geometry summary ("Link011(1/4inx1in-Screw)"; no construction recipe available for this part):
  bounding box: 29.8 x 12.8 x 11.1 mm
  tessellated surface: 2,942 triangles
  volume: 1257 mm^3 (30% of its bounding box)
  symmetry: 2-fold rotationally symmetric about the x axis; mirror-symmetric across its y mid-plane, z mid-plane
COMPONENT P12 — geometry summary ("Link012(1/4in-Nut)"; no construction recipe available for this part):
  bounding box: 12.6 x 10.9 x 4.7 mm
  tessellated surface: 2,236 triangles
  volume: 388 mm^3 (60% of its bounding box)
  symmetry: 6-fold rotationally symmetric about the x axis; 2-fold rotationally symmetric about the z axis; mirror-symmetric across its y mid-plane, z mid-plane
COMPONENT P13 — geometry summary ("1/4in-Washer "; no construction recipe available for this part):
  bounding box: 12.7 x 12.7 x 1.6 mm
  tessellated surface: 1,008 triangles
  volume: 139 mm^3 (54% of its bounding box)
  symmetry: revolution-symmetric about the z axis through its bounding-box center; mirror-symmetric across its x mid-plane, y mid-plane
COMPONENT P14 — geometry summary ("1/4inx1in-Screw "; no construction recipe available for this part):
  bounding box: 29.8 x 12.8 x 11.1 mm
  tessellated surface: 2,942 triangles
  volume: 1257 mm^3 (30% of its bounding box)
  symmetry: 3-fold rotationally symmetric about the z axis; mirror-symmetric across its x mid-plane, y mid-plane
COMPONENT P15 — geometry summary ("1/4in-Nut "; no construction recipe available for this part):
  bounding box: 12.6 x 10.9 x 4.7 mm
  tessellated surface: 2,236 triangles
  volume: 388 mm^3 (60% of its bounding box)
  symmetry: 6-fold rotationally symmetric about the x axis; 2-fold rotationally symmetric about the z axis; mirror-symmetric across its y mid-plane, z mid-plane
PROVENANCE & LICENSES
A FreeCAD (.FCStd) document from a public repository crawl; recipes are the document's own serialized feature recipes (and, for linked parts, companion documents' recipes).
License: mit.
